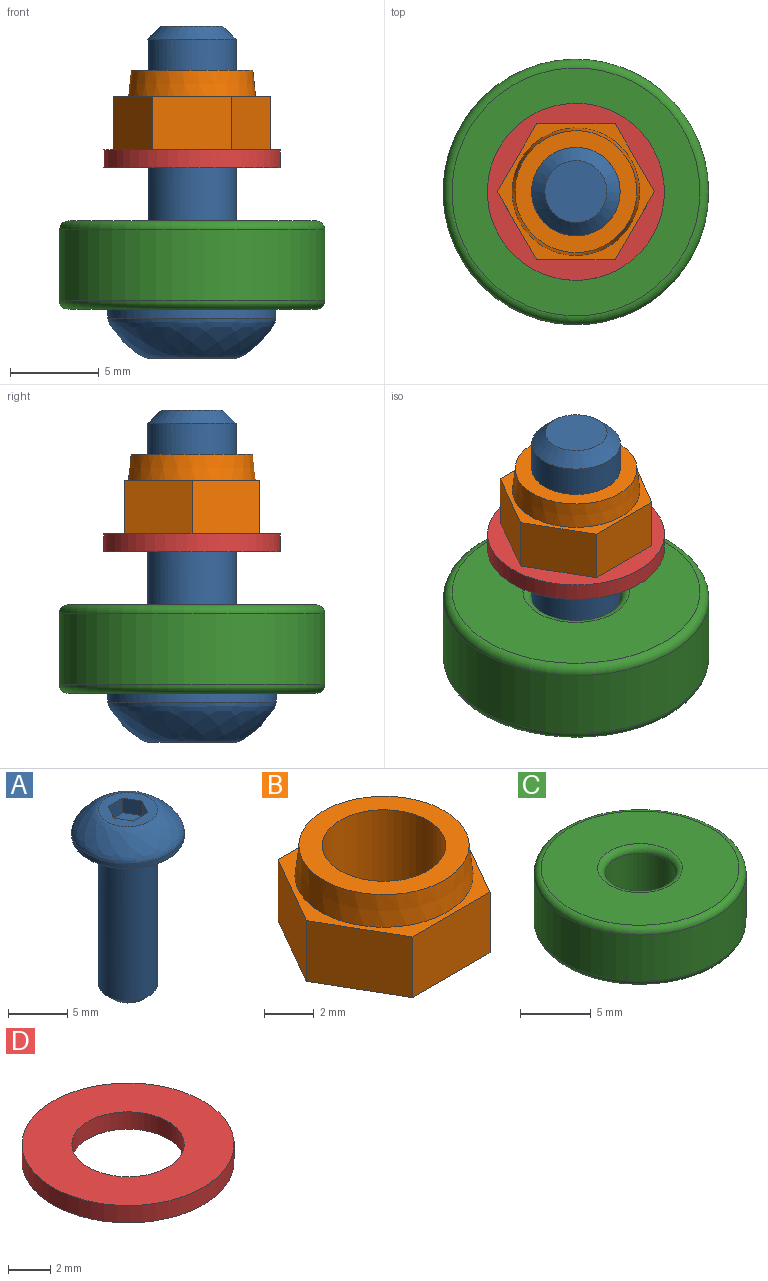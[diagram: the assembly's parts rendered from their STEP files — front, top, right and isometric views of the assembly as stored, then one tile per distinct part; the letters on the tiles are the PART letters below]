
ASSEMBLY  parts=4 mates=3
PART A: 14 faces, bbox 9.5x9.5x18.8 mm
  f0: plane 5.01x5.01mm, normal (0,0,1), area 11.8mm2, adj f3,f4,f5,f6,f7,f8,f10
  f1: cylinder r=4.75mm len=9.5mm, axis (0,0,-1), area 14.9mm2, adj f2,f10
  f2: plane 9.5x9.5mm, normal (0,0,-1), area 51.2mm2, adj f1,f11
  f3: plane 1.5x1.5mm, normal (-0.87,-0.5,0), area 2.6mm2, adj f0,f4,f8,f9
  f4: plane 1.73x1.5mm, normal (0,-1,0), area 2.6mm2, adj f0,f3,f5,f9
  f5: plane 1.5x1.5mm, normal (0.87,-0.5,0), area 2.6mm2, adj f0,f4,f6,f9
  f6: plane 1.5x1.5mm, normal (0.87,0.5,0), area 2.6mm2, adj f0,f5,f7,f9
  f7: plane 1.73x1.5mm, normal (0,1,0), area 2.6mm2, adj f0,f6,f8,f9
  f8: plane 1.5x1.5mm, normal (-0.87,0.5,0), area 2.6mm2, adj f0,f3,f7,f9
  f9: plane 3.46x3mm, normal (0,0,1), area 7.8mm2, adj f3,f4,f5,f6,f7,f8
  f10: bspline ~9.5x9.5mm, area 78.3mm2, adj f0,f1
  f11: cylinder r=2.5mm len=15.25mm, axis (0,0,1), area 239.5mm2, adj f2,f13
  f12: plane 3.5x3.5mm, normal (0,0,-1), area 9.6mm2, adj f13
  f13: cone r=1.75mm half-angle=45deg, axis (0,0,1), area 14.2mm2, adj f11,f12
PART B: 11 faces, bbox 8.9x7.7x4.5 mm
  f0: plane 3.84x3mm, normal (-0.87,0.5,0), area 13.3mm2, adj f1,f5,f6,f7
  f1: plane 3.84x3mm, normal (-0.87,-0.5,0), area 13.3mm2, adj f0,f2,f6,f7
  f2: plane 4.43x3mm, normal (0,-1,0), area 13.3mm2, adj f1,f3,f6,f7
  f3: plane 3.84x3mm, normal (0.87,-0.5,0), area 13.3mm2, adj f2,f4,f6,f7
  f4: plane 3.84x3mm, normal (0.87,0.5,0), area 13.3mm2, adj f3,f5,f6,f7
  f5: plane 4.43x3mm, normal (0,1,0), area 13.3mm2, adj f0,f4,f6,f7
  f6: plane 8.87x7.68mm, normal (0,0,1), area 10.4mm2, adj f0,f1,f2,f3,f4,f5,f8
  f7: plane 8.87x7.68mm, normal (0,0,-1), area 31.4mm2, adj f0,f1,f2,f3,f4,f5,f10
  f8: cone r=3.6mm half-angle=6deg, axis (0,0,-1), area 33.4mm2, adj f6,f9
  f9: plane 6.88x6.88mm, normal (0,0,1), area 17.6mm2, adj f8,f10
  f10: cylinder r=2.5mm len=5mm, axis (0,0,1), area 70.7mm2, adj f7,f9
PART C: 8 faces, bbox 16.2x16.2x5 mm
  f0: cylinder r=2.5mm len=5mm, axis (0,0,-1), area 62.8mm2, adj f4,f6
  f1: cylinder r=7.5mm len=15mm, axis (0,0,-1), area 188.5mm2, adj f5,f7
  f2: plane 14x14mm, normal (0,0,1), area 125.7mm2, adj f6,f7
  f3: plane 14x14mm, normal (0,0,-1), area 125.7mm2, adj f4,f5
  f4: torus R=3mm, axis (0,0,1), area 13.2mm2, adj f0,f3
  f5: torus R=7mm, axis (0,0,1), area 36.1mm2, adj f1,f3
  f6: torus R=3mm, axis (0,0,1), area 13.2mm2, adj f0,f2
  f7: torus R=7mm, axis (0,0,1), area 36.1mm2, adj f1,f2
PART D: 4 faces, bbox 10x10x1 mm
  f0: cylinder r=2.65mm len=5.3mm, axis (0,0,-1), area 16.7mm2, adj f2,f3
  f1: cylinder r=5mm len=10mm, axis (0,0,-1), area 31.4mm2, adj f2,f3
  f2: plane 10x10mm, normal (0,0,1), area 56.5mm2, adj f0,f1
  f3: plane 10x10mm, normal (0,0,-1), area 56.5mm2, adj f0,f1
PLACE A rot(axis=(1,0,0),180deg) t=(11.19,-6.82,-9.04)mm
PLACE B t=(-13.81,-6.82,-0.04)mm
PLACE C rot(axis=(1,0,0),180deg) t=(-13.81,-6.82,-4.04)mm
PLACE D t=(-13.81,-6.82,-1.04)mm
MATE fastened D.f0 <-> C.f0  axis (0,0,-1) through (-13.81,-6.82,-1.04)mm
MATE fastened D.f0 <-> B.f8  axis (0,0,1) through (-13.81,-6.82,-0.04)mm
MATE fastened C.f0 <-> A.f1  axis (0,0,-1) through (-13.81,-6.82,-9.04)mm
